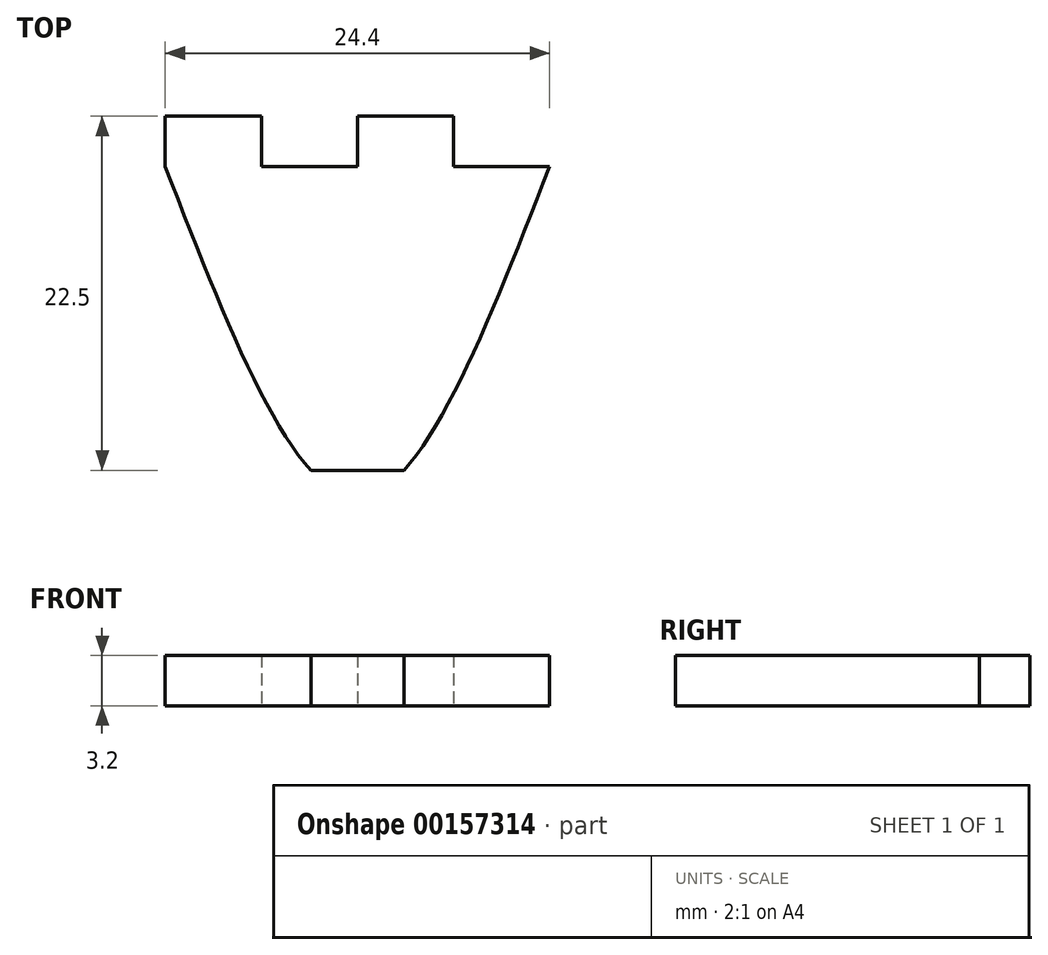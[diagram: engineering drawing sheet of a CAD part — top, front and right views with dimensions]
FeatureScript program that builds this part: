
annotation { "Feature Type Name" : "Feature", "Feature Type Description" : "" }
export const myFeature = defineFeature(function(context is Context, id is Id, definition is map)
    precondition{}
    {
        {
            var Q0;
            Q0=qCreatedBy(makeId("Top.planeOp"),FACE);
            var sketch = newSketch(context, id + "F0", { "sketchPlane" : qUnion([Q0])});
            skLineSegment(sketch, "E0", {"start": v(0, 0) * mm, "end": v(12.2, 0) * mm, "construction": true});
            skLineSegment(sketch, "E1", {"start": v(12.2, 0) * mm, "end": v(-12.2, 0) * mm, "construction": true});
            skLineSegment(sketch, "E2", {"start": v(0, 0) * mm, "end": v(0, -19.3) * mm, "construction": true});
            skFitSpline(sketch, "E3", {"points": [v(-12.2, 0) * mm, v(0, -21) * mm, v(12.2, 0) * mm], "startDerivative": vector(24.4, -63) * mm, "endDerivative": vector(24.4, 63) * mm});
            skLineSegment(sketch, "E4", {"start": v(-12.2, 0) * mm, "end": v(-12.2, 3.2) * mm});
            skLineSegment(sketch, "E5", {"start": v(-12.2, 3.2) * mm, "end": v(-6.1, 3.2) * mm});
            skLineSegment(sketch, "E6", {"start": v(-6.1, 3.2) * mm, "end": v(-6.1, 0) * mm});
            skLineSegment(sketch, "E7", {"start": v(-6.1, 0) * mm, "end": v(0, 0) * mm});
            skLineSegment(sketch, "E8", {"start": v(0, 0) * mm, "end": v(0, 3.2) * mm});
            skLineSegment(sketch, "E9", {"start": v(0, 3.2) * mm, "end": v(6.1, 3.2) * mm});
            skLineSegment(sketch, "E10", {"start": v(6.1, 3.2) * mm, "end": v(6.1, 0) * mm});
            skLineSegment(sketch, "E11", {"start": v(6.1, 0) * mm, "end": v(12.2, 0) * mm});
            skLineSegment(sketch, "E12", {"start": v(-2.96, -19.3) * mm, "end": v(2.96, -19.3) * mm});
            skSolve(sketch);
        }
        {
            var Q0;
            Q0=makeQuery(id+"F0.imprint","IMPRINT",FACE,{"disambiguationData":[TD([[makeQuery(id+"F0.imprint","IMPRINT",EDGE,{"derivedFrom":sQuery(id+"F0.wireOp",EDGE,"E3")}),1.0]])]});
            extrude(context, id + "F1", {"entities" : qUnion([Q0]), "endBound" : BoundingType.SYMMETRIC, "depth" : 3.2 * mm});
        }
    });
